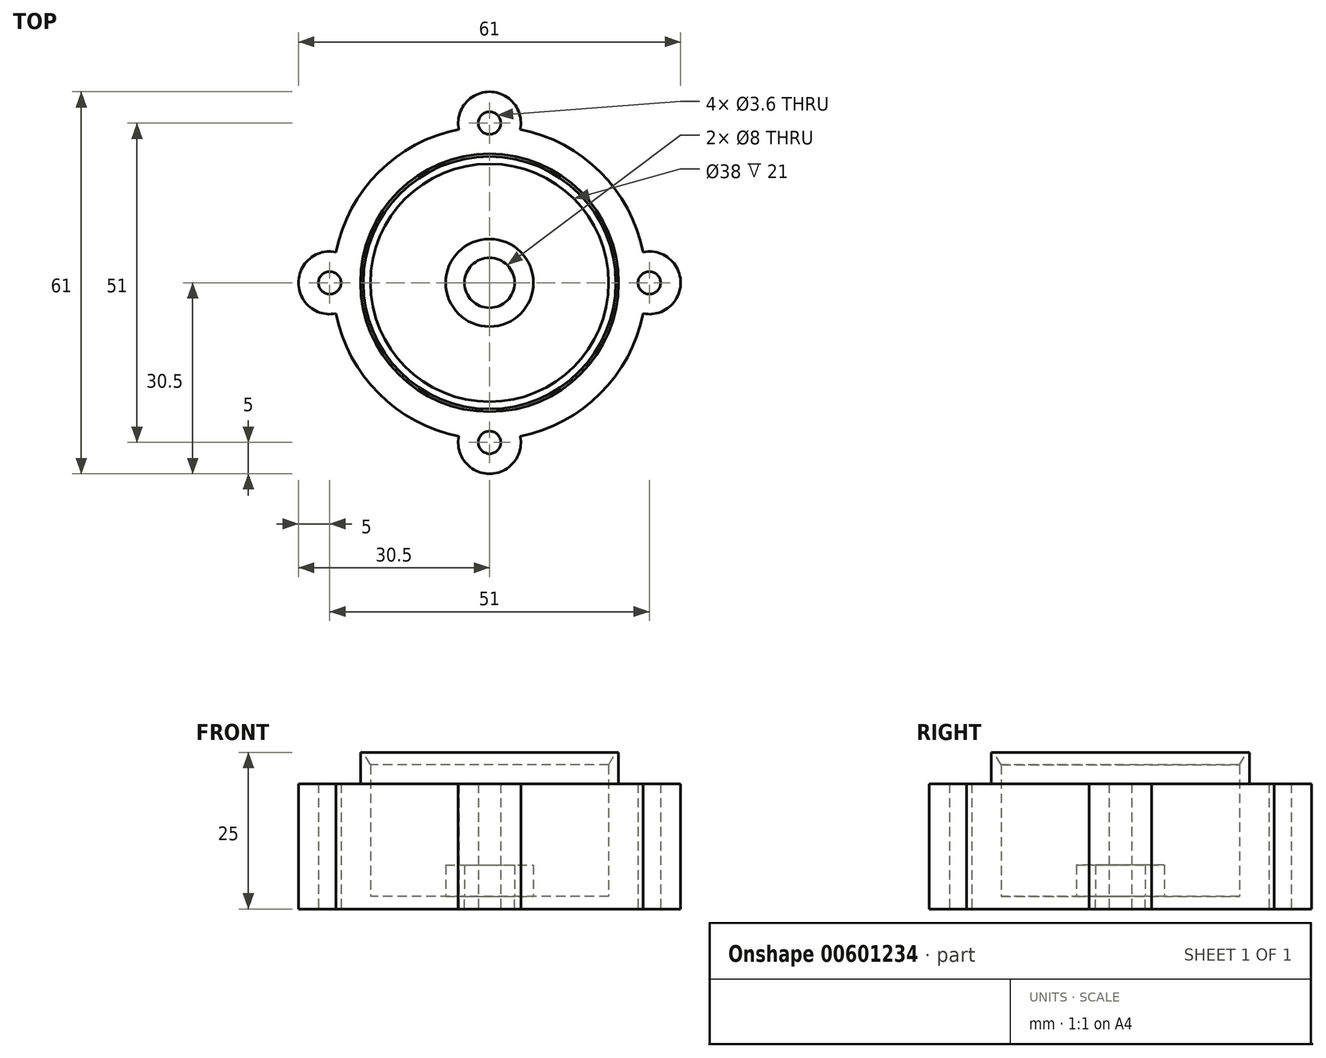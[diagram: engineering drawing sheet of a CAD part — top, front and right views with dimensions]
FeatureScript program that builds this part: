
annotation { "Feature Type Name" : "Feature", "Feature Type Description" : "" }
export const myFeature = defineFeature(function(context is Context, id is Id, definition is map)
    precondition{}
    {
        {
            var Q0;
            Q0=qCreatedBy(makeId("Top.planeOp"),FACE);
            var sketch = newSketch(context, id + "F0", { "sketchPlane" : qUnion([Q0])});
            skCircle(sketch, "E0", {"center": v(0, 0) * mm, "radius": 25 * mm});
            skCircle(sketch, "E1", {"center": v(25.5, 0) * mm, "radius": 5 * mm});
            skCircle(sketch, "E2", {"center": v(25.5, 0) * mm, "radius": 1.8 * mm});
            skCircle(sketch, "E3", {"center": v(0, 0) * mm, "radius": 19 * mm});
            skCircle(sketch, "E4.1.0", {"center": v(0, 25.5) * mm, "radius": 5 * mm});
            skCircle(sketch, "E4.1.1", {"center": v(0, 25.5) * mm, "radius": 1.8 * mm});
            skCircle(sketch, "E4.2.0", {"center": v(-25.5, 0) * mm, "radius": 5 * mm});
            skCircle(sketch, "E4.2.1", {"center": v(-25.5, 0) * mm, "radius": 1.8 * mm});
            skCircle(sketch, "E4.3.0", {"center": v(0, -25.5) * mm, "radius": 5 * mm});
            skCircle(sketch, "E4.3.1", {"center": v(0, -25.5) * mm, "radius": 1.8 * mm});
            skSolve(sketch);
        }
        {
            var Q0;
            {var subQ0=sQuery(id+"F0.wireOp",EDGE,"PekiDFlz-ehec-1jMr-j5Uu-9iqntSbjDSUp");var subQ1=sQuery(id+"F0.wireOp",EDGE,"E0");var subQ2=makeQuery(id+"F0.imprint","INTERSECT",VERTEX,{"disambiguationData":[OD(0.0)],"derivedFrom":[subQ1,subQ0]});Q0=makeQuery(id+"F0.imprint","IMPRINT",FACE,{"disambiguationData":[TD([[makeQuery(id+"F0.imprint","IMPRINT",EDGE,{"disambiguationData":[TD([[subQ2,-1.0]])],"derivedFrom":subQ1}),-1.0]])]});}
            var Q1;
            {var subQ0=sQuery(id+"F0.wireOp",EDGE,"PekiDFlz-ehec-1jMr-j5Uu-9iqntSbjDSUp");var subQ1=sQuery(id+"F0.wireOp",EDGE,"E0");var subQ2=makeQuery(id+"F0.imprint","INTERSECT",VERTEX,{"disambiguationData":[OD(0.0)],"derivedFrom":[subQ1,subQ0]});Q1=makeQuery(id+"F0.imprint","IMPRINT",FACE,{"disambiguationData":[TD([[makeQuery(id+"F0.imprint","IMPRINT",EDGE,{"disambiguationData":[TD([[subQ2,-1.0]])],"derivedFrom":subQ1}),1.0]])]});}
            var Q2;
            Q2=makeQuery(id+"F0.imprint","IMPRINT",FACE,{"disambiguationData":[TD([[makeQuery(id+"F0.imprint","IMPRINT",EDGE,{"derivedFrom":sQuery(id+"F0.wireOp",EDGE,"E3")}),-1.0]])]});
            var Q3;
            {var subQ0=sQuery(id+"F0.wireOp",EDGE,"E1");var subQ1=sQuery(id+"F0.wireOp",EDGE,"E0");var subQ2=makeQuery(id+"F0.imprint","INTERSECT",VERTEX,{"disambiguationData":[OD(0.0)],"derivedFrom":[subQ1,subQ0]});Q3=makeQuery(id+"F0.imprint","IMPRINT",FACE,{"disambiguationData":[TD([[makeQuery(id+"F0.imprint","IMPRINT",EDGE,{"disambiguationData":[TD([[subQ2,1.0]])],"derivedFrom":subQ1}),1.0]])]});}
            var Q4;
            {var subQ0=sQuery(id+"F0.wireOp",EDGE,"E1");var subQ1=sQuery(id+"F0.wireOp",EDGE,"E0");var subQ2=makeQuery(id+"F0.imprint","INTERSECT",VERTEX,{"disambiguationData":[OD(0.0)],"derivedFrom":[subQ1,subQ0]});Q4=makeQuery(id+"F0.imprint","IMPRINT",FACE,{"disambiguationData":[TD([[makeQuery(id+"F0.imprint","IMPRINT",EDGE,{"disambiguationData":[TD([[subQ2,1.0]])],"derivedFrom":subQ1}),-1.0]])]});}
            var Q5;
            {var subQ0=sQuery(id+"F0.wireOp",EDGE,"E4.3.0");var subQ1=sQuery(id+"F0.wireOp",EDGE,"E0");var subQ2=makeQuery(id+"F0.imprint","INTERSECT",VERTEX,{"disambiguationData":[OD(0.0)],"derivedFrom":[subQ1,subQ0]});Q5=makeQuery(id+"F0.imprint","IMPRINT",FACE,{"disambiguationData":[TD([[makeQuery(id+"F0.imprint","IMPRINT",EDGE,{"disambiguationData":[TD([[subQ2,-1.0]])],"derivedFrom":subQ1}),-1.0]])]});}
            var Q6;
            {var subQ0=sQuery(id+"F0.wireOp",EDGE,"E4.3.0");var subQ1=sQuery(id+"F0.wireOp",EDGE,"E0");var subQ2=makeQuery(id+"F0.imprint","INTERSECT",VERTEX,{"disambiguationData":[OD(0.0)],"derivedFrom":[subQ1,subQ0]});Q6=makeQuery(id+"F0.imprint","IMPRINT",FACE,{"disambiguationData":[TD([[makeQuery(id+"F0.imprint","IMPRINT",EDGE,{"disambiguationData":[TD([[subQ2,-1.0]])],"derivedFrom":subQ1}),1.0]])]});}
            var Q7;
            {var subQ0=sQuery(id+"F0.wireOp",EDGE,"E4.2.0");var subQ1=sQuery(id+"F0.wireOp",EDGE,"E0");var subQ2=makeQuery(id+"F0.imprint","INTERSECT",VERTEX,{"disambiguationData":[OD(0.0)],"derivedFrom":[subQ1,subQ0]});Q7=makeQuery(id+"F0.imprint","IMPRINT",FACE,{"disambiguationData":[TD([[makeQuery(id+"F0.imprint","IMPRINT",EDGE,{"disambiguationData":[TD([[subQ2,-1.0]])],"derivedFrom":subQ1}),1.0]])]});}
            var Q8;
            {var subQ0=sQuery(id+"F0.wireOp",EDGE,"E4.2.0");var subQ1=sQuery(id+"F0.wireOp",EDGE,"E0");var subQ2=makeQuery(id+"F0.imprint","INTERSECT",VERTEX,{"disambiguationData":[OD(0.0)],"derivedFrom":[subQ1,subQ0]});Q8=makeQuery(id+"F0.imprint","IMPRINT",FACE,{"disambiguationData":[TD([[makeQuery(id+"F0.imprint","IMPRINT",EDGE,{"disambiguationData":[TD([[subQ2,-1.0]])],"derivedFrom":subQ1}),-1.0]])]});}
            var Q9;
            {var subQ0=sQuery(id+"F0.wireOp",EDGE,"E4.1.0");var subQ1=sQuery(id+"F0.wireOp",EDGE,"E0");var subQ2=makeQuery(id+"F0.imprint","INTERSECT",VERTEX,{"disambiguationData":[OD(0.0)],"derivedFrom":[subQ1,subQ0]});Q9=makeQuery(id+"F0.imprint","IMPRINT",FACE,{"disambiguationData":[TD([[makeQuery(id+"F0.imprint","IMPRINT",EDGE,{"disambiguationData":[TD([[subQ2,-1.0]])],"derivedFrom":subQ1}),-1.0]])]});}
            var Q10;
            {var subQ0=sQuery(id+"F0.wireOp",EDGE,"E4.1.0");var subQ1=sQuery(id+"F0.wireOp",EDGE,"E0");var subQ2=makeQuery(id+"F0.imprint","INTERSECT",VERTEX,{"disambiguationData":[OD(0.0)],"derivedFrom":[subQ1,subQ0]});Q10=makeQuery(id+"F0.imprint","IMPRINT",FACE,{"disambiguationData":[TD([[makeQuery(id+"F0.imprint","IMPRINT",EDGE,{"disambiguationData":[TD([[subQ2,-1.0]])],"derivedFrom":subQ1}),1.0]])]});}
            extrude(context, id + "F1", {"entities" : qUnion([Q0, Q1, Q2, Q3, Q4, Q5, Q6, Q7, Q8, Q9, Q10]), "depth" : 3 * mm, "offsetDistance" : 25 * mm});
        }
        {
            var Q0;
            Q0=makeQuery(id+"F1.opExtrude","CAP_FACE",FACE,{"disambiguationData":[OSD([sQuery(id+"F0.wireOp",EDGE,"E0"),sQuery(id+"F0.wireOp",EDGE,"PekiDFlz-ehec-1jMr-j5Uu-9iqntSbjDSUp"),sQuery(id+"F0.wireOp",EDGE,"E1"),sQuery(id+"F0.wireOp",EDGE,"CFBrUIKX-aCpp-Te2x-hTl6-JWUO2pwLkCTu"),sQuery(id+"F0.wireOp",EDGE,"E2"),sQuery(id+"F0.wireOp",EDGE,"E3")])],"isStart":false});
            var sketch = newSketch(context, id + "F2", { "sketchPlane" : qUnion([Q0])});
            skCircle(sketch, "E5", {"center": v(0, 0) * mm, "radius": 19 * mm});
            skCircle(sketch, "E6", {"center": v(0, 0) * mm, "radius": 20.6 * mm});
            skSolve(sketch);
        }
        {
            var Q0;
            Q0=makeQuery(id+"F2.imprint","IMPRINT",FACE,{"disambiguationData":[TD([[makeQuery(id+"F2.imprint","IMPRINT",EDGE,{"derivedFrom":sQuery(id+"F2.wireOp",EDGE,"E5")}),-1.0]])]});
            extrude(context, id + "F3", {"entities" : qUnion([Q0]), "operationType" : NewBodyOperationType.ADD, "depth" : 5 * mm, "offsetDistance" : 25 * mm});
        }
        {
            var Q0;
            Q0=makeQuery(id+"F3.opExtrude","CAP_EDGE",EDGE,{"disambiguationData":[OSD([sQuery(id+"F2.wireOp",EDGE,"E5")])],"isStart":false});
            chamfer(context, id + "F4", {"entities" : qUnion([Q0]), "chamferType" : ChamferType.OFFSET_ANGLE, "width" : 2 * mm, "oppositeDirection" : false, "angle" : 30 * degree, "tangentPropagation" : true});
        }
        {
            var Q0;
            Q0=makeQuery(id+"F0.imprint","IMPRINT",FACE,{"disambiguationData":[TD([[makeQuery(id+"F0.imprint","IMPRINT",EDGE,{"derivedFrom":sQuery(id+"F0.wireOp",EDGE,"E3")}),-1.0]])]});
            var Q1;
            {var subQ0=sQuery(id+"F0.wireOp",EDGE,"E4.2.0");var subQ1=sQuery(id+"F0.wireOp",EDGE,"E0");var subQ2=makeQuery(id+"F0.imprint","INTERSECT",VERTEX,{"disambiguationData":[OD(0.0)],"derivedFrom":[subQ1,subQ0]});Q1=makeQuery(id+"F0.imprint","IMPRINT",FACE,{"disambiguationData":[TD([[makeQuery(id+"F0.imprint","IMPRINT",EDGE,{"disambiguationData":[TD([[subQ2,-1.0]])],"derivedFrom":subQ1}),-1.0]])]});}
            var Q2;
            {var subQ0=sQuery(id+"F0.wireOp",EDGE,"E4.2.0");var subQ1=sQuery(id+"F0.wireOp",EDGE,"E0");var subQ2=makeQuery(id+"F0.imprint","INTERSECT",VERTEX,{"disambiguationData":[OD(0.0)],"derivedFrom":[subQ1,subQ0]});Q2=makeQuery(id+"F0.imprint","IMPRINT",FACE,{"disambiguationData":[TD([[makeQuery(id+"F0.imprint","IMPRINT",EDGE,{"disambiguationData":[TD([[subQ2,-1.0]])],"derivedFrom":subQ1}),1.0]])]});}
            var Q3;
            {var subQ0=sQuery(id+"F0.wireOp",EDGE,"E4.3.0");var subQ1=sQuery(id+"F0.wireOp",EDGE,"E0");var subQ2=makeQuery(id+"F0.imprint","INTERSECT",VERTEX,{"disambiguationData":[OD(0.0)],"derivedFrom":[subQ1,subQ0]});Q3=makeQuery(id+"F0.imprint","IMPRINT",FACE,{"disambiguationData":[TD([[makeQuery(id+"F0.imprint","IMPRINT",EDGE,{"disambiguationData":[TD([[subQ2,-1.0]])],"derivedFrom":subQ1}),1.0]])]});}
            var Q4;
            {var subQ0=sQuery(id+"F0.wireOp",EDGE,"E4.3.0");var subQ1=sQuery(id+"F0.wireOp",EDGE,"E0");var subQ2=makeQuery(id+"F0.imprint","INTERSECT",VERTEX,{"disambiguationData":[OD(0.0)],"derivedFrom":[subQ1,subQ0]});Q4=makeQuery(id+"F0.imprint","IMPRINT",FACE,{"disambiguationData":[TD([[makeQuery(id+"F0.imprint","IMPRINT",EDGE,{"disambiguationData":[TD([[subQ2,-1.0]])],"derivedFrom":subQ1}),-1.0]])]});}
            var Q5;
            {var subQ0=sQuery(id+"F0.wireOp",EDGE,"E1");var subQ1=sQuery(id+"F0.wireOp",EDGE,"E0");var subQ2=makeQuery(id+"F0.imprint","INTERSECT",VERTEX,{"disambiguationData":[OD(0.0)],"derivedFrom":[subQ1,subQ0]});Q5=makeQuery(id+"F0.imprint","IMPRINT",FACE,{"disambiguationData":[TD([[makeQuery(id+"F0.imprint","IMPRINT",EDGE,{"disambiguationData":[TD([[subQ2,1.0]])],"derivedFrom":subQ1}),1.0]])]});}
            var Q6;
            {var subQ0=sQuery(id+"F0.wireOp",EDGE,"E1");var subQ1=sQuery(id+"F0.wireOp",EDGE,"E0");var subQ2=makeQuery(id+"F0.imprint","INTERSECT",VERTEX,{"disambiguationData":[OD(0.0)],"derivedFrom":[subQ1,subQ0]});Q6=makeQuery(id+"F0.imprint","IMPRINT",FACE,{"disambiguationData":[TD([[makeQuery(id+"F0.imprint","IMPRINT",EDGE,{"disambiguationData":[TD([[subQ2,1.0]])],"derivedFrom":subQ1}),-1.0]])]});}
            var Q7;
            {var subQ0=sQuery(id+"F0.wireOp",EDGE,"E4.1.0");var subQ1=sQuery(id+"F0.wireOp",EDGE,"E0");var subQ2=makeQuery(id+"F0.imprint","INTERSECT",VERTEX,{"disambiguationData":[OD(0.0)],"derivedFrom":[subQ1,subQ0]});Q7=makeQuery(id+"F0.imprint","IMPRINT",FACE,{"disambiguationData":[TD([[makeQuery(id+"F0.imprint","IMPRINT",EDGE,{"disambiguationData":[TD([[subQ2,-1.0]])],"derivedFrom":subQ1}),1.0]])]});}
            var Q8;
            {var subQ0=sQuery(id+"F0.wireOp",EDGE,"E4.1.0");var subQ1=sQuery(id+"F0.wireOp",EDGE,"E0");var subQ2=makeQuery(id+"F0.imprint","INTERSECT",VERTEX,{"disambiguationData":[OD(0.0)],"derivedFrom":[subQ1,subQ0]});Q8=makeQuery(id+"F0.imprint","IMPRINT",FACE,{"disambiguationData":[TD([[makeQuery(id+"F0.imprint","IMPRINT",EDGE,{"disambiguationData":[TD([[subQ2,-1.0]])],"derivedFrom":subQ1}),-1.0]])]});}
            extrude(context, id + "F5", {"entities" : qUnion([Q0, Q1, Q2, Q3, Q4, Q5, Q6, Q7, Q8]), "operationType" : NewBodyOperationType.ADD, "oppositeDirection" : true, "depth" : 15 * mm, "offsetDistance" : 25 * mm});
        }
        {
            var Q0;
            Q0=makeQuery(id+"F5.opExtrude","CAP_FACE",FACE,{"disambiguationData":[OSD([sQuery(id+"F0.wireOp",EDGE,"E0"),sQuery(id+"F0.wireOp",EDGE,"E1"),sQuery(id+"F0.wireOp",EDGE,"E3"),sQuery(id+"F0.wireOp",EDGE,"E4.1.0"),sQuery(id+"F0.wireOp",EDGE,"E4.2.0"),sQuery(id+"F0.wireOp",EDGE,"E4.3.0")])],"isStart":false});
            var sketch = newSketch(context, id + "F6", { "sketchPlane" : qUnion([Q0])});
            skCircle(sketch, "E7", {"center": v(0, 0) * mm, "radius": 4 * mm});
            skCircle(sketch, "E8", {"center": v(0, 0) * mm, "radius": 7 * mm});
            skSolve(sketch);
        }
        {
            var Q0;
            {var subQ2=sQuery(id+"F0.wireOp",EDGE,"E1");Q0=makeQuery(id+"F6.imprint","IMPRINT",FACE,{"disambiguationData":[TD([[makeQuery(id+"F6.imprint","IMPRINT",EDGE,{"derivedFrom":makeQuery(id+"F5.opExtrude","CAP_EDGE",EDGE,{"disambiguationData":[OSD([subQ2])],"isStart":false})}),1.0]])]});}
            var Q1;
            Q1=makeQuery(id+"F6.imprint","IMPRINT",FACE,{"disambiguationData":[TD([[makeQuery(id+"F6.imprint","IMPRINT",EDGE,{"derivedFrom":sQuery(id+"F6.wireOp",EDGE,"E8")}),-1.0]])]});
            var Q2;
            Q2=makeQuery(id+"F6.imprint","IMPRINT",FACE,{"disambiguationData":[TD([[makeQuery(id+"F6.imprint","IMPRINT",EDGE,{"derivedFrom":sQuery(id+"F6.wireOp",EDGE,"E7")}),-1.0]])]});
            var Q3;
            {var subQ2=sQuery(id+"F0.wireOp",EDGE,"E1");Q3=makeQuery(id+"F6.imprint","IMPRINT",FACE,{"disambiguationData":[TD([[makeQuery(id+"F6.imprint","IMPRINT",EDGE,{"derivedFrom":makeQuery(id+"F5.opExtrude","CAP_EDGE",EDGE,{"disambiguationData":[OSD([subQ2])],"isStart":false})}),-1.0]])]});}
            extrude(context, id + "F7", {"entities" : qUnion([Q0, Q1, Q2, Q3]), "operationType" : NewBodyOperationType.ADD, "depth" : 2 * mm, "offsetDistance" : 25 * mm});
        }
        {
            var Q0;
            Q0=makeQuery(id+"F6.imprint","IMPRINT",FACE,{"disambiguationData":[TD([[makeQuery(id+"F6.imprint","IMPRINT",EDGE,{"derivedFrom":sQuery(id+"F6.wireOp",EDGE,"E7")}),-1.0]])]});
            extrude(context, id + "F8", {"entities" : qUnion([Q0]), "oppositeDirection" : true, "depth" : 5 * mm, "offsetDistance" : 25 * mm});
        }
    });
